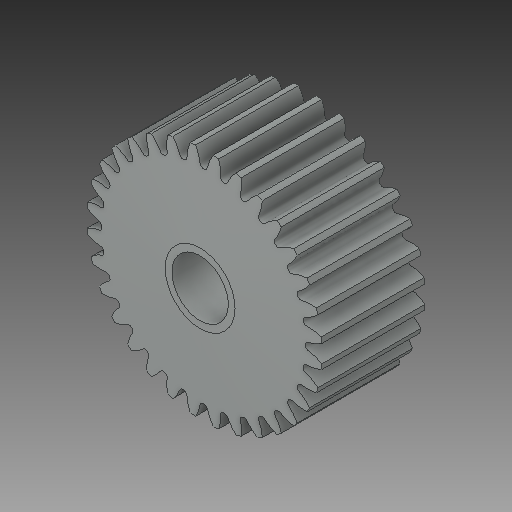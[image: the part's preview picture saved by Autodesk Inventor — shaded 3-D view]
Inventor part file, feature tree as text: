
AUTODESK INVENTOR PART (.ipt)
format: ipt  version: 2018 (Build 220112000, 112)  size: 512,000 bytes
history: native  units: in
note: dims shown in document units (in); Inventor stores cm internally (conversion verified against a paired STEP export)
features: mirror x1
ambient origin geometry x8: Origin, YZ Plane, XZ Plane, XY Plane, X Axis, Y Axis, Z Axis, Center Point
bodies: Solid1 (feature_tree)
feature tree (1):
  mirror  "Mirror1"
